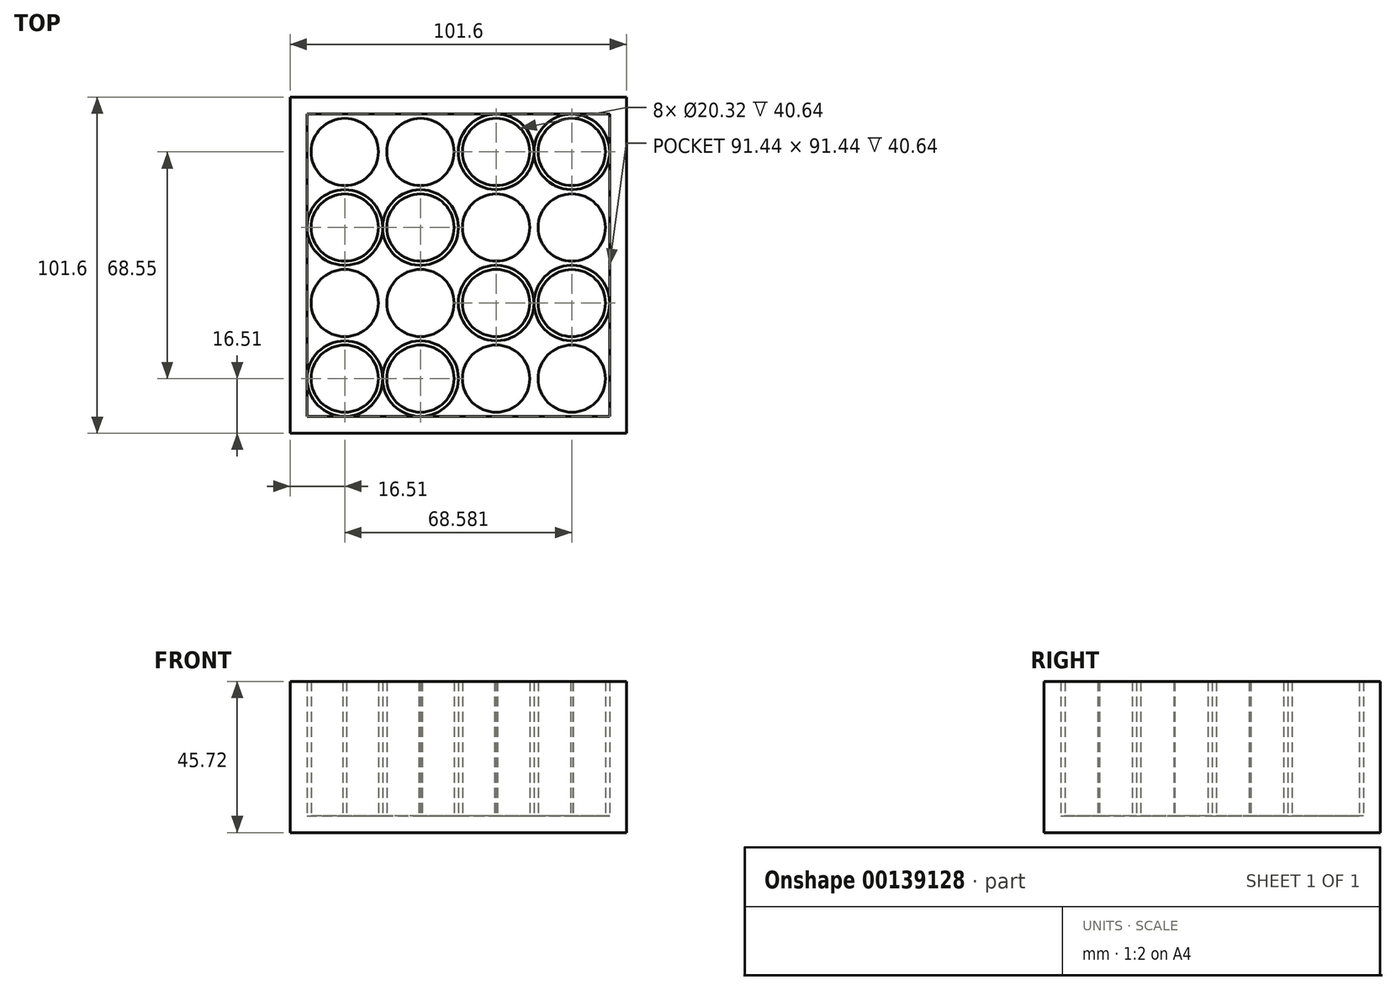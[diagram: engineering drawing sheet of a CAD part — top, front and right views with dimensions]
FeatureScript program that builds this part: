
annotation { "Feature Type Name" : "Feature", "Feature Type Description" : "" }
export const myFeature = defineFeature(function(context is Context, id is Id, definition is map)
    precondition{}
    {
        {
            var Q0;
            Q0=qCreatedBy(makeId("Top.planeOp"),FACE);
            var sketch = newSketch(context, id + "F0", { "sketchPlane" : qUnion([Q0])});
            skLineSegment(sketch, "E0.bottom", {"start": v(0, 0) * mm, "end": v(91.44, 0) * mm});
            skLineSegment(sketch, "E0.top", {"start": v(0, -91.44) * mm, "end": v(91.44, -91.44) * mm});
            skLineSegment(sketch, "E0.left", {"start": v(0, 0) * mm, "end": v(0, -91.44) * mm});
            skLineSegment(sketch, "E0.right", {"start": v(91.44, 0) * mm, "end": v(91.44, -91.44) * mm});
            skLineSegment(sketch, "E1", {"start": v(0, 0) * mm, "end": v(0, 5.08) * mm});
            skLineSegment(sketch, "E2", {"start": v(0, 5.08) * mm, "end": v(-5.08, 5.08) * mm});
            skLineSegment(sketch, "E3.bottom", {"start": v(-5.08, 5.08) * mm, "end": v(96.52, 5.08) * mm});
            skLineSegment(sketch, "E3.top", {"start": v(-5.08, -96.52) * mm, "end": v(96.52, -96.52) * mm});
            skLineSegment(sketch, "E3.left", {"start": v(-5.08, 5.08) * mm, "end": v(-5.08, -96.52) * mm});
            skLineSegment(sketch, "E3.right", {"start": v(96.52, 5.08) * mm, "end": v(96.52, -96.52) * mm});
            skSolve(sketch);
        }
        {
            var Q0;
            Q0=makeQuery(id+"F0.imprint","IMPRINT",FACE,{"disambiguationData":[TD([[makeQuery(id+"F0.imprint","IMPRINT",EDGE,{"derivedFrom":sQuery(id+"F0.wireOp",EDGE,"E0.bottom")}),1.0]])]});
            extrude(context, id + "F1", {"entities" : qUnion([Q0]), "depth" : 45.72 * mm});
        }
        {
            var Q0;
            Q0=qCreatedBy(makeId("Top.planeOp"),FACE);
            var sketch = newSketch(context, id + "F2", { "sketchPlane" : qUnion([Q0])});
            skLineSegment(sketch, "E4.bottom", {"start": v(0, 0) * mm, "end": v(91.44, 0) * mm});
            skLineSegment(sketch, "E4.top", {"start": v(0, -91.44) * mm, "end": v(91.44, -91.44) * mm});
            skLineSegment(sketch, "E4.left", {"start": v(0, 0) * mm, "end": v(0, -91.44) * mm});
            skLineSegment(sketch, "E4.right", {"start": v(91.44, 0) * mm, "end": v(91.44, -91.44) * mm});
            skSolve(sketch);
        }
        {
            var Q0;
            Q0=makeQuery(id+"F2.imprint","IMPRINT",FACE,{"disambiguationData":[TD([[makeQuery(id+"F2.imprint","IMPRINT",EDGE,{"derivedFrom":sQuery(id+"F2.wireOp",EDGE,"E4.bottom")}),-1.0]])]});
            extrude(context, id + "F3", {"entities" : qUnion([Q0]), "operationType" : NewBodyOperationType.ADD, "depth" : 5.08 * mm});
        }
        {
            var Q0;
            Q0=makeQuery(id+"F3.opExtrude","CAP_FACE",FACE,{"disambiguationData":[OSD([sQuery(id+"F2.wireOp",EDGE,"E4.bottom"),sQuery(id+"F2.wireOp",EDGE,"E4.top"),sQuery(id+"F2.wireOp",EDGE,"E4.left"),sQuery(id+"F2.wireOp",EDGE,"E4.right")])],"isStart":false});
            var sketch = newSketch(context, id + "F4", { "sketchPlane" : qUnion([Q0])});
            skLineSegment(sketch, "E5", {"start": v(0, -91.44) * mm, "end": v(0, -80.01) * mm});
            skCircle(sketch, "E6", {"center": v(11.43, -80) * mm, "radius": 11.43 * mm});
            skCircle(sketch, "E7", {"center": v(11.43, -80) * mm, "radius": 10.16 * mm});
            skCircle(sketch, "E8", {"center": v(34.3, -80.01) * mm, "radius": 11.43 * mm});
            skCircle(sketch, "E9", {"center": v(34.3, -80.01) * mm, "radius": 10.16 * mm});
            skLineSegment(sketch, "E10", {"start": v(45.72, -79.86) * mm, "end": v(45.72, -53.5) * mm});
            skLineSegment(sketch, "E11", {"start": v(45.72, -53.5) * mm, "end": v(45.72, -91.44) * mm});
            skCircle(sketch, "E12.MirrorC", {"center": v(80, -80) * mm, "radius": 11.43 * mm});
            skCircle(sketch, "E13.MirrorC", {"center": v(57.15, -80) * mm, "radius": 10.16 * mm});
            skCircle(sketch, "E14.MirrorC", {"center": v(57.15, -80) * mm, "radius": 11.43 * mm});
            skCircle(sketch, "E15.MirrorC", {"center": v(80, -80) * mm, "radius": 10.16 * mm});
            skLineSegment(sketch, "E16.MirrorCS", {"start": v(91.44, -91.44) * mm, "end": v(91.44, -80) * mm});
            skLineSegment(sketch, "E17", {"start": v(33.97, -68.58) * mm, "end": v(91.44, -68.58) * mm});
            skLineSegment(sketch, "E18", {"start": v(91.44, -68.58) * mm, "end": v(0, -68.58) * mm});
            skLineSegment(sketch, "E19.MirrorCS", {"start": v(45.72, -57.3) * mm, "end": v(45.72, -83.66) * mm});
            skCircle(sketch, "E20.MirrorC", {"center": v(57.15, -57.16) * mm, "radius": 11.43 * mm});
            skCircle(sketch, "E21.MirrorC", {"center": v(57.15, -57.16) * mm, "radius": 10.16 * mm});
            skCircle(sketch, "E22.MirrorC", {"center": v(34.3, -57.15) * mm, "radius": 10.16 * mm});
            skCircle(sketch, "E23.MirrorC", {"center": v(11.43, -57.15) * mm, "radius": 10.16 * mm});
            skCircle(sketch, "E24.MirrorC", {"center": v(80.01, -57.16) * mm, "radius": 10.16 * mm});
            skCircle(sketch, "E25.MirrorC", {"center": v(80.01, -57.16) * mm, "radius": 11.43 * mm});
            skCircle(sketch, "E26.MirrorC", {"center": v(34.3, -57.15) * mm, "radius": 11.43 * mm});
            skCircle(sketch, "E27.MirrorC", {"center": v(11.43, -57.15) * mm, "radius": 11.43 * mm});
            skLineSegment(sketch, "E28.MirrorCS", {"start": v(45.72, -83.66) * mm, "end": v(45.72, -45.72) * mm});
            skLineSegment(sketch, "E29", {"start": v(56.85, -45.73) * mm, "end": v(91.44, -45.73) * mm});
            skLineSegment(sketch, "E30", {"start": v(91.44, -45.73) * mm, "end": v(2.76, -45.73) * mm});
            skLineSegment(sketch, "E31.MirrorCS", {"start": v(45.72, -11.61) * mm, "end": v(45.72, -37.97) * mm});
            skLineSegment(sketch, "E32.MirrorCS", {"start": v(45.72, -34.16) * mm, "end": v(45.72, -7.8) * mm});
            skLineSegment(sketch, "E33.MirrorCS", {"start": v(45.72, -7.8) * mm, "end": v(45.72, -45.75) * mm});
            skCircle(sketch, "E34.MirrorC", {"center": v(57.15, -11.46) * mm, "radius": 11.43 * mm});
            skCircle(sketch, "E35.MirrorC", {"center": v(34.3, -34.32) * mm, "radius": 11.43 * mm});
            skCircle(sketch, "E36.MirrorC", {"center": v(57.15, -11.46) * mm, "radius": 10.16 * mm});
            skCircle(sketch, "E37.MirrorC", {"center": v(80, -11.46) * mm, "radius": 11.43 * mm});
            skLineSegment(sketch, "E38.MirrorCS", {"start": v(45.72, -37.97) * mm, "end": v(45.72, -0.03) * mm});
            skCircle(sketch, "E39.MirrorC", {"center": v(34.29, -11.46) * mm, "radius": 10.16 * mm});
            skCircle(sketch, "E40.MirrorC", {"center": v(34.29, -11.46) * mm, "radius": 11.43 * mm});
            skCircle(sketch, "E41.MirrorC", {"center": v(11.43, -11.46) * mm, "radius": 10.16 * mm});
            skCircle(sketch, "E42.MirrorC", {"center": v(11.43, -11.46) * mm, "radius": 11.43 * mm});
            skCircle(sketch, "E43.MirrorC", {"center": v(80, -11.46) * mm, "radius": 10.16 * mm});
            skCircle(sketch, "E44.MirrorC", {"center": v(57.15, -34.31) * mm, "radius": 10.16 * mm});
            skCircle(sketch, "E45.MirrorC", {"center": v(11.43, -34.32) * mm, "radius": 11.43 * mm});
            skCircle(sketch, "E46.MirrorC", {"center": v(80.01, -34.3) * mm, "radius": 11.43 * mm});
            skCircle(sketch, "E47.MirrorC", {"center": v(57.15, -34.31) * mm, "radius": 11.43 * mm});
            skLineSegment(sketch, "E48.MirrorCS", {"start": v(91.44, -22.89) * mm, "end": v(0, -22.9) * mm});
            skLineSegment(sketch, "E49.MirrorCS", {"start": v(33.97, -22.89) * mm, "end": v(91.44, -22.89) * mm});
            skCircle(sketch, "E50.MirrorC", {"center": v(11.43, -34.32) * mm, "radius": 10.16 * mm});
            skCircle(sketch, "E51.MirrorC", {"center": v(34.3, -34.32) * mm, "radius": 10.16 * mm});
            skCircle(sketch, "E52.MirrorC", {"center": v(80.01, -34.3) * mm, "radius": 10.16 * mm});
            skSolve(sketch);
        }
        {
            var Q0;
            Q0=makeQuery(id+"F4.imprint","IMPRINT",FACE,{"disambiguationData":[TD([[makeQuery(id+"F4.imprint","IMPRINT",EDGE,{"derivedFrom":sQuery(id+"F4.wireOp",EDGE,"E41.MirrorC")}),1.0]])]});
            var Q1;
            Q1=makeQuery(id+"F4.imprint","IMPRINT",FACE,{"disambiguationData":[TD([[makeQuery(id+"F4.imprint","IMPRINT",EDGE,{"derivedFrom":sQuery(id+"F4.wireOp",EDGE,"E39.MirrorC")}),1.0]])]});
            var Q2;
            Q2=makeQuery(id+"F4.imprint","IMPRINT",FACE,{"disambiguationData":[TD([[makeQuery(id+"F4.imprint","IMPRINT",EDGE,{"derivedFrom":sQuery(id+"F4.wireOp",EDGE,"E36.MirrorC")}),-1.0]])]});
            var Q3;
            Q3=makeQuery(id+"F4.imprint","IMPRINT",FACE,{"disambiguationData":[TD([[makeQuery(id+"F4.imprint","IMPRINT",EDGE,{"derivedFrom":sQuery(id+"F4.wireOp",EDGE,"E43.MirrorC")}),-1.0]])]});
            var Q4;
            Q4=makeQuery(id+"F4.imprint","IMPRINT",FACE,{"disambiguationData":[TD([[makeQuery(id+"F4.imprint","IMPRINT",EDGE,{"derivedFrom":sQuery(id+"F4.wireOp",EDGE,"E50.MirrorC")}),-1.0]])]});
            var Q5;
            Q5=makeQuery(id+"F4.imprint","IMPRINT",FACE,{"disambiguationData":[TD([[makeQuery(id+"F4.imprint","IMPRINT",EDGE,{"derivedFrom":sQuery(id+"F4.wireOp",EDGE,"E51.MirrorC")}),-1.0]])]});
            var Q6;
            Q6=makeQuery(id+"F4.imprint","IMPRINT",FACE,{"disambiguationData":[TD([[makeQuery(id+"F4.imprint","IMPRINT",EDGE,{"derivedFrom":sQuery(id+"F4.wireOp",EDGE,"E44.MirrorC")}),1.0]])]});
            var Q7;
            Q7=makeQuery(id+"F4.imprint","IMPRINT",FACE,{"disambiguationData":[TD([[makeQuery(id+"F4.imprint","IMPRINT",EDGE,{"derivedFrom":sQuery(id+"F4.wireOp",EDGE,"E52.MirrorC")}),1.0]])]});
            var Q8;
            Q8=makeQuery(id+"F4.imprint","IMPRINT",FACE,{"disambiguationData":[TD([[makeQuery(id+"F4.imprint","IMPRINT",EDGE,{"derivedFrom":sQuery(id+"F4.wireOp",EDGE,"E24.MirrorC")}),-1.0]])]});
            var Q9;
            Q9=makeQuery(id+"F4.imprint","IMPRINT",FACE,{"disambiguationData":[TD([[makeQuery(id+"F4.imprint","IMPRINT",EDGE,{"derivedFrom":sQuery(id+"F4.wireOp",EDGE,"E21.MirrorC")}),-1.0]])]});
            var Q10;
            Q10=makeQuery(id+"F4.imprint","IMPRINT",FACE,{"disambiguationData":[TD([[makeQuery(id+"F4.imprint","IMPRINT",EDGE,{"derivedFrom":sQuery(id+"F4.wireOp",EDGE,"E22.MirrorC")}),1.0]])]});
            var Q11;
            Q11=makeQuery(id+"F4.imprint","IMPRINT",FACE,{"disambiguationData":[TD([[makeQuery(id+"F4.imprint","IMPRINT",EDGE,{"derivedFrom":sQuery(id+"F4.wireOp",EDGE,"E23.MirrorC")}),1.0]])]});
            var Q12;
            Q12=makeQuery(id+"F4.imprint","IMPRINT",FACE,{"disambiguationData":[TD([[makeQuery(id+"F4.imprint","IMPRINT",EDGE,{"derivedFrom":sQuery(id+"F4.wireOp",EDGE,"E7")}),-1.0]])]});
            var Q13;
            Q13=makeQuery(id+"F4.imprint","IMPRINT",FACE,{"disambiguationData":[TD([[makeQuery(id+"F4.imprint","IMPRINT",EDGE,{"derivedFrom":sQuery(id+"F4.wireOp",EDGE,"E9")}),-1.0]])]});
            var Q14;
            Q14=makeQuery(id+"F4.imprint","IMPRINT",FACE,{"disambiguationData":[TD([[makeQuery(id+"F4.imprint","IMPRINT",EDGE,{"derivedFrom":sQuery(id+"F4.wireOp",EDGE,"E13.MirrorC")}),1.0]])]});
            var Q15;
            Q15=makeQuery(id+"F4.imprint","IMPRINT",FACE,{"disambiguationData":[TD([[makeQuery(id+"F4.imprint","IMPRINT",EDGE,{"derivedFrom":sQuery(id+"F4.wireOp",EDGE,"E15.MirrorC")}),1.0]])]});
            extrude(context, id + "F5", {"entities" : qUnion([Q0, Q1, Q2, Q3, Q4, Q5, Q6, Q7, Q8, Q9, Q10, Q11, Q12, Q13, Q14, Q15]), "depth" : 40.64 * mm});
        }
    });
